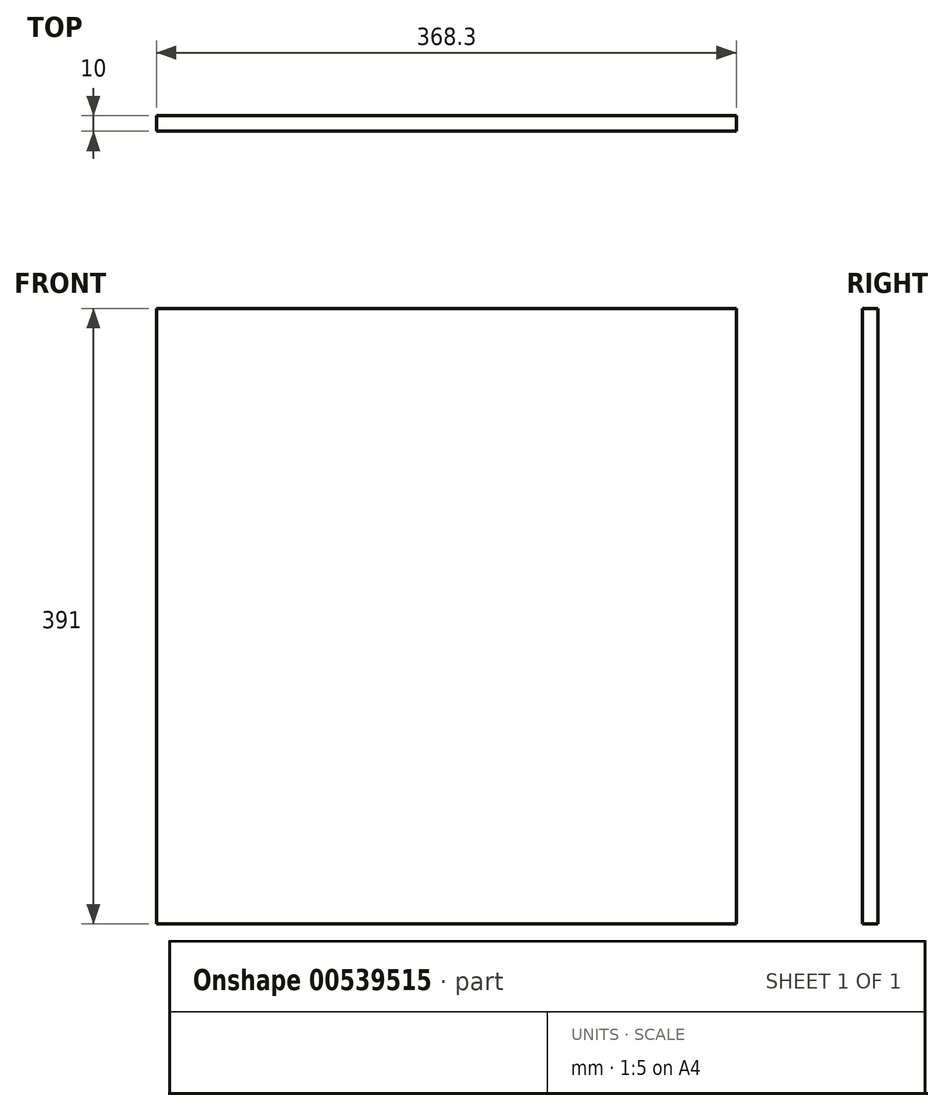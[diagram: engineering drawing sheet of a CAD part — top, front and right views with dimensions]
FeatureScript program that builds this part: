
annotation { "Feature Type Name" : "Feature", "Feature Type Description" : "" }
export const myFeature = defineFeature(function(context is Context, id is Id, definition is map)
    precondition{}
    {
        {
            var Q0;
            Q0=qCreatedBy(makeId("Front.planeOp"),FACE);
            var sketch = newSketch(context, id + "F0", { "sketchPlane" : qUnion([Q0])});
            skLineSegment(sketch, "E0.bottom", {"start": v(184.15, -195.5) * mm, "end": v(-184.15, -195.5) * mm});
            skLineSegment(sketch, "E0.top", {"start": v(184.15, 195.5) * mm, "end": v(-184.15, 195.5) * mm});
            skLineSegment(sketch, "E0.left", {"start": v(184.15, -195.5) * mm, "end": v(184.15, 195.5) * mm});
            skLineSegment(sketch, "E0.right", {"start": v(-184.15, -195.5) * mm, "end": v(-184.15, 195.5) * mm});
            skPoint(sketch, "E0.middle", {"position": v(0, 0) * mm});
            skSolve(sketch);
        }
        {
            var Q0;
            Q0=makeQuery(id+"F0.imprint","IMPRINT",FACE,{"disambiguationData":[TD([[makeQuery(id+"F0.imprint","IMPRINT",EDGE,{"derivedFrom":sQuery(id+"F0.wireOp",EDGE,"E0.bottom")}),-1.0]])]});
            extrude(context, id + "F1", {"entities" : qUnion([Q0]), "depth" : 10 * mm});
        }
    });
